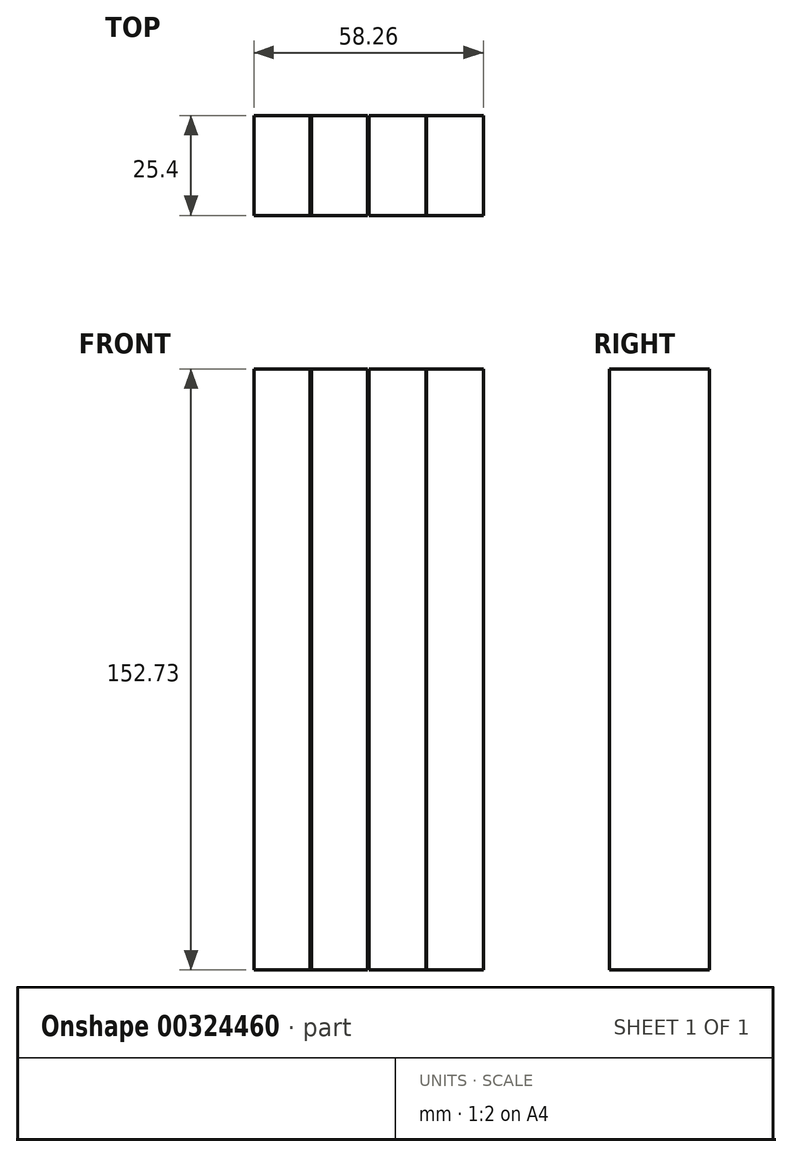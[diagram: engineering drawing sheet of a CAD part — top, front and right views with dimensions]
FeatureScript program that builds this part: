
annotation { "Feature Type Name" : "Feature", "Feature Type Description" : "" }
export const myFeature = defineFeature(function(context is Context, id is Id, definition is map)
    precondition{}
    {
        {
            var Q0;
            Q0=qCreatedBy(makeId("Front.planeOp"),FACE);
            var sketch = newSketch(context, id + "F0", { "sketchPlane" : qUnion([Q0])});
            skLineSegment(sketch, "E0.bottom", {"start": v(-75.83, 75.96) * mm, "end": v(-61.26, 75.96) * mm});
            skLineSegment(sketch, "E0.top", {"start": v(-75.83, -76.77) * mm, "end": v(-61.26, -76.77) * mm});
            skLineSegment(sketch, "E0.left", {"start": v(-75.83, 75.96) * mm, "end": v(-75.83, -76.77) * mm});
            skLineSegment(sketch, "E0.right", {"start": v(-61.26, 75.96) * mm, "end": v(-61.26, -76.77) * mm});
            skSolve(sketch);
        }
        {
            var Q0;
            Q0 = qSketchRegion(id + "F0", true);
            extrude(context, id + "F1", {"entities" : qUnion([Q0]), "depth" : 25.4 * mm});
        }
        {
            var Q0;
            Q0=makeQuery(id+"F1.opExtrude","SWEPT_BODY",BODY,{"disambiguationData":[OSD([sQuery(id+"F0.wireOp",EDGE,"E0.bottom"),sQuery(id+"F0.wireOp",EDGE,"E0.top"),sQuery(id+"F0.wireOp",EDGE,"E0.left"),sQuery(id+"F0.wireOp",EDGE,"E0.right")])]});
            transform(context, id + "F2", {"entities" : qUnion([Q0]), "transformType" : TransformType.TRANSLATION_3D, "dx" : 14.22 * mm, "dy" : 0 * mm, "dz" : 0 * mm, "makeCopy" : true});
        }
        {
            var Q0;
            Q0=makeQuery(id+"F2.opPattern","COPY",BODY,{"derivedFrom":makeQuery(id+"F1.opExtrude","SWEPT_BODY",BODY,{"disambiguationData":[OSD([sQuery(id+"F0.wireOp",EDGE,"E0.bottom"),sQuery(id+"F0.wireOp",EDGE,"E0.top"),sQuery(id+"F0.wireOp",EDGE,"E0.left"),sQuery(id+"F0.wireOp",EDGE,"E0.right")])]}),"instanceName":"1"});
            transform(context, id + "F3", {"entities" : qUnion([Q0]), "transformType" : TransformType.TRANSLATION_3D, "dx" : 15 * mm, "dy" : 0 * mm, "dz" : 0 * mm, "makeCopy" : true});
        }
        {
            var Q0;
            Q0=makeQuery(id+"F3.opPattern","COPY",BODY,{"derivedFrom":makeQuery(id+"F2.opPattern","COPY",BODY,{"derivedFrom":makeQuery(id+"F1.opExtrude","SWEPT_BODY",BODY,{"disambiguationData":[OSD([sQuery(id+"F0.wireOp",EDGE,"E0.bottom"),sQuery(id+"F0.wireOp",EDGE,"E0.top"),sQuery(id+"F0.wireOp",EDGE,"E0.left"),sQuery(id+"F0.wireOp",EDGE,"E0.right")])]}),"instanceName":"1"}),"instanceName":"1"});
            transform(context, id + "F4", {"entities" : qUnion([Q0]), "transformType" : TransformType.TRANSLATION_3D, "dx" : 14.48 * mm, "dy" : 0 * mm, "dz" : 0 * mm, "makeCopy" : true});
        }
    });
